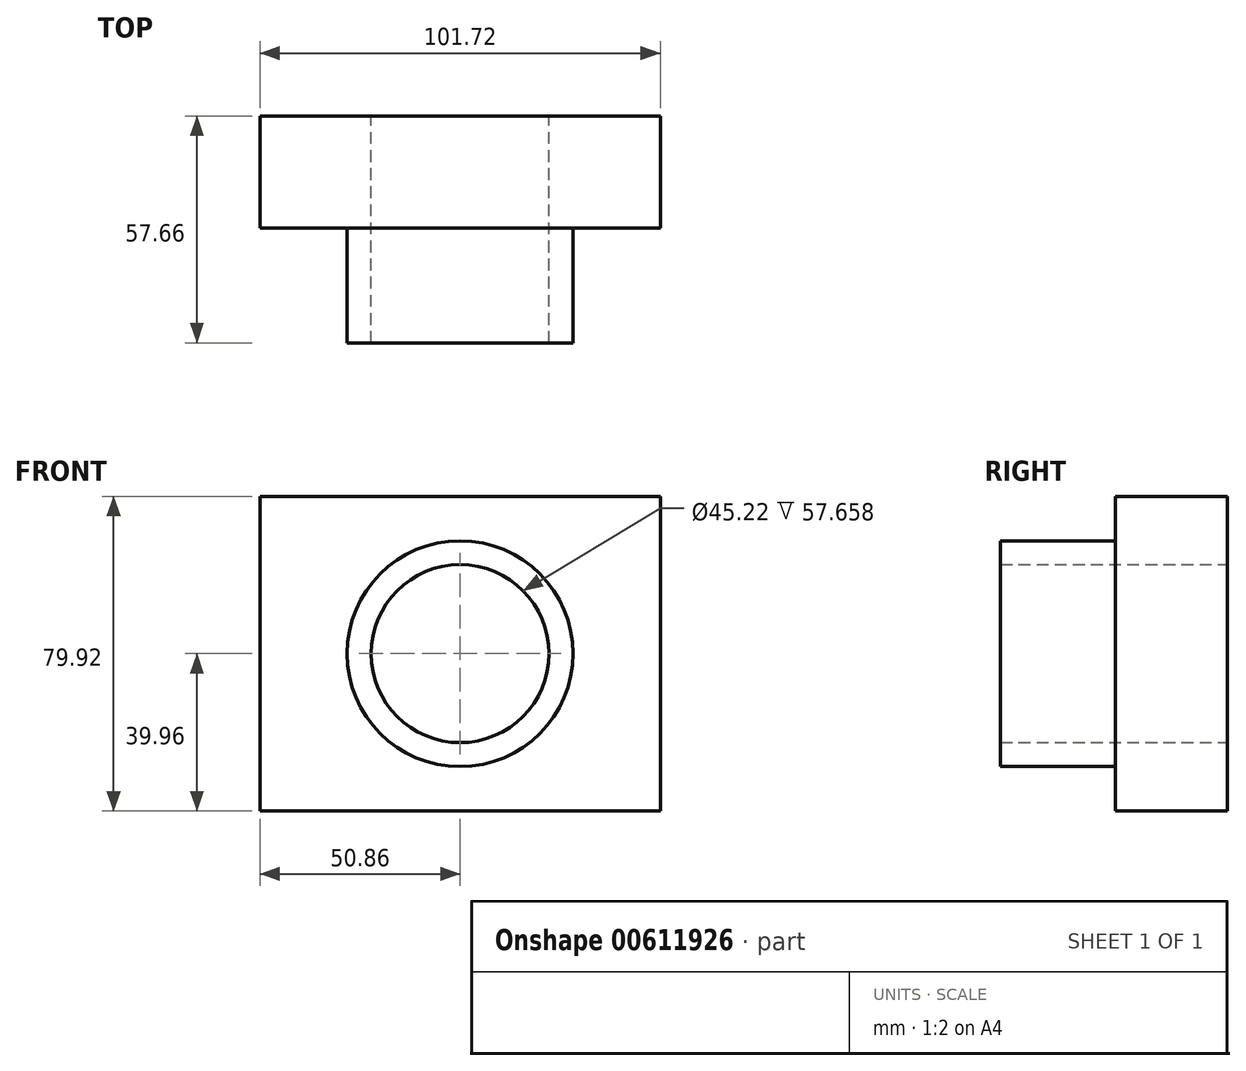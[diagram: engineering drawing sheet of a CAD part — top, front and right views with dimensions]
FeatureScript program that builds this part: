
annotation { "Feature Type Name" : "Feature", "Feature Type Description" : "" }
export const myFeature = defineFeature(function(context is Context, id is Id, definition is map)
    precondition{}
    {
        {
            var Q0;
            Q0=qCreatedBy(makeId("Front.planeOp"),FACE);
            var sketch = newSketch(context, id + "F0", { "sketchPlane" : qUnion([Q0])});
            skLineSegment(sketch, "E0.bottom", {"start": v(-50.86, 39.96) * mm, "end": v(50.86, 39.96) * mm});
            skLineSegment(sketch, "E0.top", {"start": v(-50.86, -39.96) * mm, "end": v(50.86, -39.96) * mm});
            skLineSegment(sketch, "E0.left", {"start": v(-50.86, 39.96) * mm, "end": v(-50.86, -39.96) * mm});
            skLineSegment(sketch, "E0.right", {"start": v(50.86, 39.96) * mm, "end": v(50.86, -39.96) * mm});
            skPoint(sketch, "E0.middle", {"position": v(0, 0) * mm});
            skSolve(sketch);
        }
        {
            var Q0;
            Q0 = qSketchRegion(id + "F0", true);
            extrude(context, id + "F1", {"entities" : qUnion([Q0]), "depth" : 28.45 * mm, "offsetDistance" : 25.4 * mm});
        }
        {
            var Q0;
            Q0=qCreatedBy(makeId("Front.planeOp"),FACE);
            var sketch = newSketch(context, id + "F2", { "sketchPlane" : qUnion([Q0])});
            skCircle(sketch, "E1", {"center": v(0, 0) * mm, "radius": 28.69 * mm});
            skSolve(sketch);
        }
        {
            var Q0;
            Q0 = qSketchRegion(id + "F2", true);
            extrude(context, id + "F3", {"entities" : qUnion([Q0]), "operationType" : NewBodyOperationType.ADD, "depth" : 57.66 * mm, "offsetDistance" : 25.4 * mm});
        }
        {
            var Q0;
            Q0=qCreatedBy(makeId("Front.planeOp"),FACE);
            var sketch = newSketch(context, id + "F4", { "sketchPlane" : qUnion([Q0])});
            skCircle(sketch, "E2", {"center": v(0, 0) * mm, "radius": 22.6 * mm});
            skSolve(sketch);
        }
        {
            var Q0;
            Q0 = qSketchRegion(id + "F4", true);
            extrude(context, id + "F5", {"entities" : qUnion([Q0]), "operationType" : NewBodyOperationType.REMOVE, "depth" : 70.87 * mm, "offsetDistance" : 25.4 * mm});
        }
    });
